# Revit family: XPD-Supply
name_source: partatom
category: Mechanical Equipment
units: mm (PartAtom-declared; Revit-internal decimal feet)

## family parameters
Always vertical = Yes
Cut with Voids When Loaded = No
Part Type = Normal
Room Calculation Point = No
Round Connector Dimension = Use Diameter
Shared = No
Work Plane-Based = No

## types (8) — shared parameters
(E-C)/2 = 0' - 1"
-D = -0' - 2"
0 = 0' - 0"
1" = 0' - 1"
1.5 = 0' - 1 1/2"
1/2 = 0' - 0 1/2"
135 = 135.00°
2" = 0' - 2"
2' = 2' - 0"
3" = 0' - 3"
4" = 0' - 4"
9" = 0' - 9"
90 = 90.00°
EMINUSC = 0' - 2"
Manufacturer = Loren Cook Company
Model = SPD
ONE EIGTH = 0' - 0 1/8"
Type Comments = Packaged Propeller Wall Exhaust Fan Direct Drive
URL = www.lorencook.com

## per-type parameters (varying)
- 12_XPD-Supply: (A/2)-1"=0' - 7 27/32"; (A/2)-C-.5"=0' - 5 27/32"; (D-.25")/2=0' - 6 1/8"; (SIZE/2)-.25"=0' - 5 3/4"; -((A/2)-C-.5")=-0' - 5 27/32"; -((SIZE/2)-.25")=-0' - 5 3/4"; -B=-0' - 7 1/2"; -B+1"=-0' - 6 1/2"; -C/2=-0' - 0 7/8"; -SPD_D/2=-0' - 8 7/8"; -WH_B/2=-0' - 11"; A=1' - 4 3/16"; A/2=0' - 8 3/32"; A/3.5=0' - 4 5/8"; A/7=0' - 2 5/16"; B=0' - 7 1/2"; B/2=0' - 3 3/4"; C=0' - 1 3/4"; C+F=0' - 2 13/16"; C/2=0' - 0 7/8"; D=1' - 0 1/2"; D/2=0' - 6 1/4"; F=0' - 1 1/16"; RO=1' - 5 1/4"; SIZE=1' - 0"; SIZE/2=0' - 6"; SPD_A=1' - 7 1/2"; SPD_A/2=0' - 9 3/4"; SPD_B=1' - 5"; SPD_B/2=0' - 8 1/2"; SPD_C=1' - 2"; SPD_C/2=0' - 7"; SPD_D=1' - 5 3/4"; SPD_D/2=0' - 8 7/8"; WH_A=1' - 6 11/16"; WH_B=1' - 10"; WH_B/2=0' - 11"; WH_C=2' - 1"
- 16_XPD-Supply: (A/2)-1"=0' - 9 27/32"; (A/2)-C-.5"=0' - 7 3/32"; (D-.25")/2=0' - 8 1/8"; (SIZE/2)-.25"=0' - 7 3/4"; -((A/2)-C-.5")=-0' - 7 3/32"; -((SIZE/2)-.25")=-0' - 7 3/4"; -B=-0' - 8 1/2"; -B+1"=-0' - 7 1/2"; -C/2=-0' - 1 1/4"; -SPD_D/2=-0' - 11 1/8"; -WH_B/2=-1' - 1"; A=1' - 8 3/16"; A/2=0' - 10 3/32"; A/3.5=0' - 5 25/32"; A/7=0' - 2 7/8"; B=0' - 8 1/2"; B/2=0' - 4 1/4"; C=0' - 2 1/2"; C+F=0' - 3 3/4"; C/2=0' - 1 1/4"; D=1' - 4 1/2"; D/2=0' - 8 1/4"; F=0' - 1 1/4"; RO=1' - 9 1/4"; SIZE=1' - 4"; SIZE/2=0' - 8"; SPD_A=1' - 11 1/2"; SPD_A/2=0' - 11 3/4"; SPD_B=1' - 9"; SPD_B/2=0' - 10 1/2"; SPD_C=1' - 6"; SPD_C/2=0' - 9"; SPD_D=1' - 10 1/4"; SPD_D/2=0' - 11 1/8"; WH_A=1' - 9 11/16"; WH_B=2' - 2"; WH_B/2=1' - 1"; WH_C=2' - 5"
- 20_XPD-Supply: (A/2)-1"=0' - 11 27/32"; (A/2)-C-.5"=0' - 8 27/32"; (D-.25")/2=0' - 10 3/16"; (SIZE/2)-.25"=0' - 9 3/4"; -((A/2)-C-.5")=-0' - 8 27/32"; -((SIZE/2)-.25")=-0' - 9 3/4"; -B=-0' - 9 3/4"; -B+1"=-0' - 8 3/4"; -C/2=-0' - 1 3/8"; -SPD_D/2=-0' - 11 5/8"; -WH_B/2=-1' - 3"; A=2' - 0 3/16"; A/2=1' - 0 3/32"; A/3.5=0' - 6 29/32"; A/7=0' - 3 15/32"; B=0' - 9 3/4"; B/2=0' - 4 7/8"; C=0' - 2 3/4"; C+F=0' - 4 1/8"; C/2=0' - 1 3/8"; D=1' - 8 5/8"; D/2=0' - 10 5/16"; F=0' - 1 3/8"; RO=2' - 1 1/4"; SIZE=1' - 8"; SIZE/2=0' - 10"; SPD_A=2' - 3 1/2"; SPD_A/2=1' - 1 3/4"; SPD_B=2' - 1"; SPD_B/2=1' - 0 1/2"; SPD_C=1' - 10"; SPD_C/2=0' - 11"; SPD_D=1' - 11 1/4"; SPD_D/2=0' - 11 5/8"; WH_A=2' - 0 3/8"; WH_B=2' - 6"; WH_B/2=1' - 3"; WH_C=2' - 9"
- 24_XPD-Supply: (A/2)-1"=1' - 2 27/32"; (A/2)-C-.5"=0' - 11 27/32"; (D-.25")/2=1' - 0 1/4"; (SIZE/2)-.25"=0' - 11 3/4"; -((A/2)-C-.5")=-0' - 11 27/32"; -((SIZE/2)-.25")=-0' - 11 3/4"; -B=-0' - 9 3/4"; -B+1"=-0' - 8 3/4"; -C/2=-0' - 1 3/8"; -SPD_D/2=-0' - 11 5/8"; -WH_B/2=-1' - 5"; A=2' - 6 3/16"; A/2=1' - 3 3/32"; A/3.5=0' - 8 5/8"; A/7=0' - 4 5/16"; B=0' - 9 3/4"; B/2=0' - 4 7/8"; C=0' - 2 3/4"; C+F=0' - 4 1/16"; C/2=0' - 1 3/8"; D=2' - 0 3/4"; D/2=1' - 0 3/8"; F=0' - 1 5/16"; RO=2' - 7 1/4"; SIZE=2' - 0"; SIZE/2=1' - 0"; SPD_A=2' - 9 1/2"; SPD_A/2=1' - 4 3/4"; SPD_B=2' - 7"; SPD_B/2=1' - 3 1/2"; SPD_C=2' - 3 1/2"; SPD_C/2=1' - 1 3/4"; SPD_D=1' - 11 1/4"; SPD_D/2=0' - 11 5/8"; WH_A=2' - 3 1/8"; WH_B=2' - 10"; WH_B/2=1' - 5"; WH_C=3' - 1"
- 14_XPD-Supply: (A/2)-1"=0' - 9 27/32"; (A/2)-C-.5"=0' - 7 3/32"; (D-.25")/2=0' - 7 1/8"; (SIZE/2)-.25"=0' - 6 3/4"; -((A/2)-C-.5")=-0' - 7 3/32"; -((SIZE/2)-.25")=-0' - 6 3/4"; -B=-0' - 8 1/2"; -B+1"=-0' - 7 1/2"; -C/2=-0' - 1 1/4"; -SPD_D/2=-0' - 11 1/8"; -WH_B/2=-1' - 1"; A=1' - 8 3/16"; A/2=0' - 10 3/32"; A/3.5=0' - 5 25/32"; A/7=0' - 2 7/8"; B=0' - 8 1/2"; B/2=0' - 4 1/4"; C=0' - 2 1/2"; C+F=0' - 3 7/8"; C/2=0' - 1 1/4"; D=1' - 2 1/2"; D/2=0' - 7 1/4"; F=0' - 1 3/8"; RO=1' - 9 1/4"; SIZE=1' - 2"; SIZE/2=0' - 7"; SPD_A=1' - 11 1/2"; SPD_A/2=0' - 11 3/4"; SPD_B=1' - 9"; SPD_B/2=0' - 10 1/2"; SPD_C=1' - 6"; SPD_C/2=0' - 9"; SPD_D=1' - 10 1/4"; SPD_D/2=0' - 11 1/8"; WH_A=1' - 9 11/16"; WH_B=2' - 2"; WH_B/2=1' - 1"; WH_C=2' - 5"
- 18_XPD-Supply: (A/2)-1"=0' - 11 27/32"; (A/2)-C-.5"=0' - 8 27/32"; (D-.25")/2=0' - 9 1/8"; (SIZE/2)-.25"=0' - 8 3/4"; -((A/2)-C-.5")=-0' - 8 27/32"; -((SIZE/2)-.25")=-0' - 8 3/4"; -B=-0' - 9 3/4"; -B+1"=-0' - 8 3/4"; -C/2=-0' - 1 3/8"; -SPD_D/2=-0' - 11 5/8"; -WH_B/2=-1' - 3"; A=2' - 0 3/16"; A/2=1' - 0 3/32"; A/3.5=0' - 6 29/32"; A/7=0' - 3 15/32"; B=0' - 9 3/4"; B/2=0' - 4 7/8"; C=0' - 2 3/4"; C+F=0' - 4"; C/2=0' - 1 3/8"; D=1' - 6 1/2"; D/2=0' - 9 1/4"; F=0' - 1 1/4"; RO=2' - 1 1/4"; SIZE=1' - 6"; SIZE/2=0' - 9"; SPD_A=2' - 3 1/2"; SPD_A/2=1' - 1 3/4"; SPD_B=2' - 1"; SPD_B/2=1' - 0 1/2"; SPD_C=1' - 10"; SPD_C/2=0' - 11"; SPD_D=1' - 11 1/4"; SPD_D/2=0' - 11 5/8"; WH_A=2' - 0 3/8"; WH_B=2' - 6"; WH_B/2=1' - 3"; WH_C=2' - 9"
- 10_XPD-Supply: (A/2)-1"=0' - 7 27/32"; (A/2)-C-.5"=0' - 6 3/32"; (D-.25")/2=0' - 5 1/8"; (SIZE/2)-.25"=0' - 4 3/4"; -((A/2)-C-.5")=-0' - 6 3/32"; -((SIZE/2)-.25")=-0' - 4 3/4"; -B=-0' - 5 1/2"; -B+1"=-0' - 4 1/2"; -C/2=-0' - 0 3/4"; -SPD_D/2=-0' - 8 7/8"; -WH_B/2=-0' - 11"; A=1' - 4 3/16"; A/2=0' - 8 3/32"; A/3.5=0' - 4 5/8"; A/7=0' - 2 5/16"; B=0' - 5 1/2"; B/2=0' - 2 3/4"; C=0' - 1 1/2"; C+F=0' - 2 5/8"; C/2=0' - 0 3/4"; D=0' - 10 1/2"; D/2=0' - 5 1/4"; F=0' - 1 1/8"; RO=1' - 5 1/4"; SIZE=0' - 10"; SIZE/2=0' - 5"; SPD_A=1' - 7 1/2"; SPD_A/2=0' - 9 3/4"; SPD_B=1' - 5"; SPD_B/2=0' - 8 1/2"; SPD_C=1' - 2"; SPD_C/2=0' - 7"; SPD_D=1' - 5 3/4"; SPD_D/2=0' - 8 7/8"; WH_A=1' - 6 11/16"; WH_B=1' - 10"; WH_B/2=0' - 11"; WH_C=2' - 1"
- 8_XPD-Supply: (A/2)-1"=0' - 5 27/32"; (A/2)-C-.5"=0' - 4 19/32"; (D-.25")/2=0' - 4 1/8"; (SIZE/2)-.25"=0' - 3 3/4"; -((A/2)-C-.5")=-0' - 4 19/32"; -((SIZE/2)-.25")=-0' - 3 3/4"; -B=-0' - 4 3/4"; -B+1"=-0' - 3 3/4"; -C/2=-0' - 0 1/2"; -SPD_D/2=-0' - 6 7/8"; -WH_B/2=-0' - 9"; A=1' - 0 3/16"; A/2=0' - 6 3/32"; A/3.5=0' - 3 15/32"; A/7=0' - 1 3/4"; B=0' - 4 3/4"; B/2=0' - 2 3/8"; C=0' - 1"; C+F=0' - 1 1/2"; C/2=0' - 0 1/2"; D=0' - 8 1/2"; D/2=0' - 4 1/4"; F=0' - 0 1/2"; RO=1' - 1 1/4"; SIZE=0' - 8"; SIZE/2=0' - 4"; SPD_A=1' - 3 1/2"; SPD_A/2=0' - 7 3/4"; SPD_B=1' - 1"; SPD_B/2=0' - 6 1/2"; SPD_C=0' - 10"; SPD_C/2=0' - 5"; SPD_D=1' - 1 3/4"; SPD_D/2=0' - 6 7/8"; WH_A=1' - 3 13/16"; WH_B=1' - 6"; WH_B/2=0' - 9"; WH_C=1' - 9"

## geometry (parser evidence)
native form markers: Sweep x2
no freeform markers — native parametric forms only
